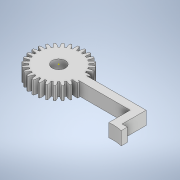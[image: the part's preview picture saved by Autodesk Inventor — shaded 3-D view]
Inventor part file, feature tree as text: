
AUTODESK INVENTOR PART (.ipt)
format: ipt  version: 2022 (Build 260153000, 153)  size: 361,984 bytes
history: native  units: in
note: dims shown in document units (in); Inventor stores cm internally (conversion verified against a paired STEP export)
features: sketch x9, extrude x8, pattern_circular x1
ambient origin geometry x8: Origin, YZ Plane, XZ Plane, XY Plane, X Axis, Y Axis, Z Axis, Center Point
bodies: Solid1 (feature_tree)
feature tree (18):
  extrude  "Extrusion1"  Depth=0.1575in
  pattern_circular  "Circular Pattern1"  Count=28 Angle=360.0deg
  extrude  "Extrusion6"  Depth=0.0787in
  extrude  "Extrusion7"  Depth=0.0787in TaperAngle=0.0deg
  extrude  "Extrusion8"  Depth=0.0787in
  extrude  "Extrusion9"  Depth=0.0787in
  extrude  "Extrusion10"  Depth=0.0787in
  extrude  "Extrusion11"  Depth=0.0787in
  extrude  "Extrusion12"  Depth=0.1969in
  sketch  "Sketch17"  dims[d49=0.1969in d50=0.1575in d51=0.5438in d52=0.0in d53=1.1811in d54=0.7087in d55=0.748in d56=0.748in d57=0.1969in d58=0.9843in d59=0.0591in d60=0.0591in d61=0.0591in d62=0.3543in d63=0.0591in d64=0.1181in d65=0.1969in d66=0.0197in d67=0.0197in d68=0.0197in d69=0.1969in d70=0.0in d71=1.1811in d72=0.3543in d73=0.1181in d74=0.1181in d75=0.3543in d76=0.1181in d77=0.1969in d78=0.0197in d79=0.1969in d80=0.0197in d81=0.0197in d82=0.1969in d83=0.0in d84=0.2938in d85=0.0in d93=1.1811in d94=0.3937in d95=0.9843in d96=1.2205in d97=0.3543in d98=0.1181in d99=0.1181in d100=0.0787in d101=0.1181in d102=0.0787in d103=0.1969in d104=0.0in d105=0.0787in d106=0.0787in d107=0.3031in d108=0.0in d109=0.0394in d110=0.5094in d111=0.0in]
  sketch  "Sketch1"  dims[d0=0.6299in d1=0.1575in]
  sketch  "Sketch8"  dims[d2=0.0098in]
  sketch  "Sketch9"  dims[d3=0.0098in]
  sketch  "Sketch10"  dims[d4=0.0236in]
  sketch  "Sketch11"  dims[d7=0.0472in]
  sketch  "Sketch14"  dims[d8=0.1772in]
  sketch  "Sketch15"  dims[d10=0.0787in]
  sketch  "Sketch16"  dims[d11=0.1969in d12=0.0in d13=11.0236in d14=360.0deg]
